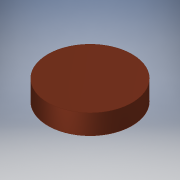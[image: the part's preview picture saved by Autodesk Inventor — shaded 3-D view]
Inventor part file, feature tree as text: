
AUTODESK INVENTOR PART (.ipt)
format: ipt  version: 2018 (Build 220112000, 112)  size: 91,136 bytes
history: native  units: in
note: dims shown in document units (in); Inventor stores cm internally (conversion verified against a paired STEP export)
features: extrude x1, sketch x1
ambient origin geometry x8: Origin, YZ Plane, XZ Plane, XY Plane, X Axis, Y Axis, Z Axis, Center Point
bodies: Solid1 (feature_tree)
feature tree (2):
  extrude  "Extrusion1"  Depth=0.25in TaperAngle=0.0deg
  sketch  "Sketch1"  dims[d0=1.05in d1=0.25in d2=0.0in]
